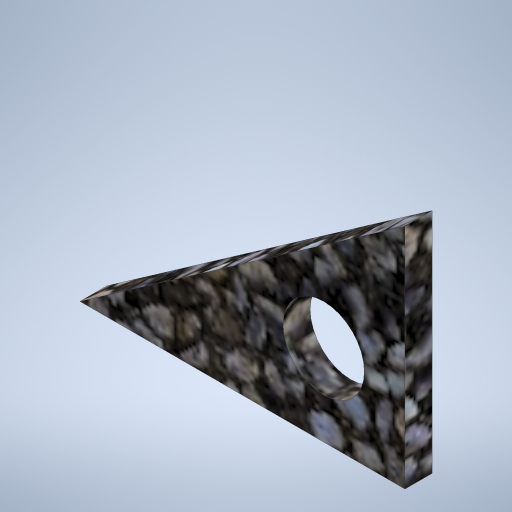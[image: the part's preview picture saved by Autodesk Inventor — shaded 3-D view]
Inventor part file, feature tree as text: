
AUTODESK INVENTOR PART (.ipt)
format: ipt  version: 2024 (Build 280153000, 153)  size: 363,520 bytes
history: native  units: in
note: dims shown in document units (in); Inventor stores cm internally (conversion verified against a paired STEP export)
features: extrude x1, other x1
ambient origin geometry x8: Origin, YZ Plane, XZ Plane, XY Plane, X Axis, Y Axis, Z Axis, Center Point
bodies: Solid1 (feature_tree)
feature tree (2):
  extrude  "triangle extrusion"  Depth=3.0in
  other  "triangle"
